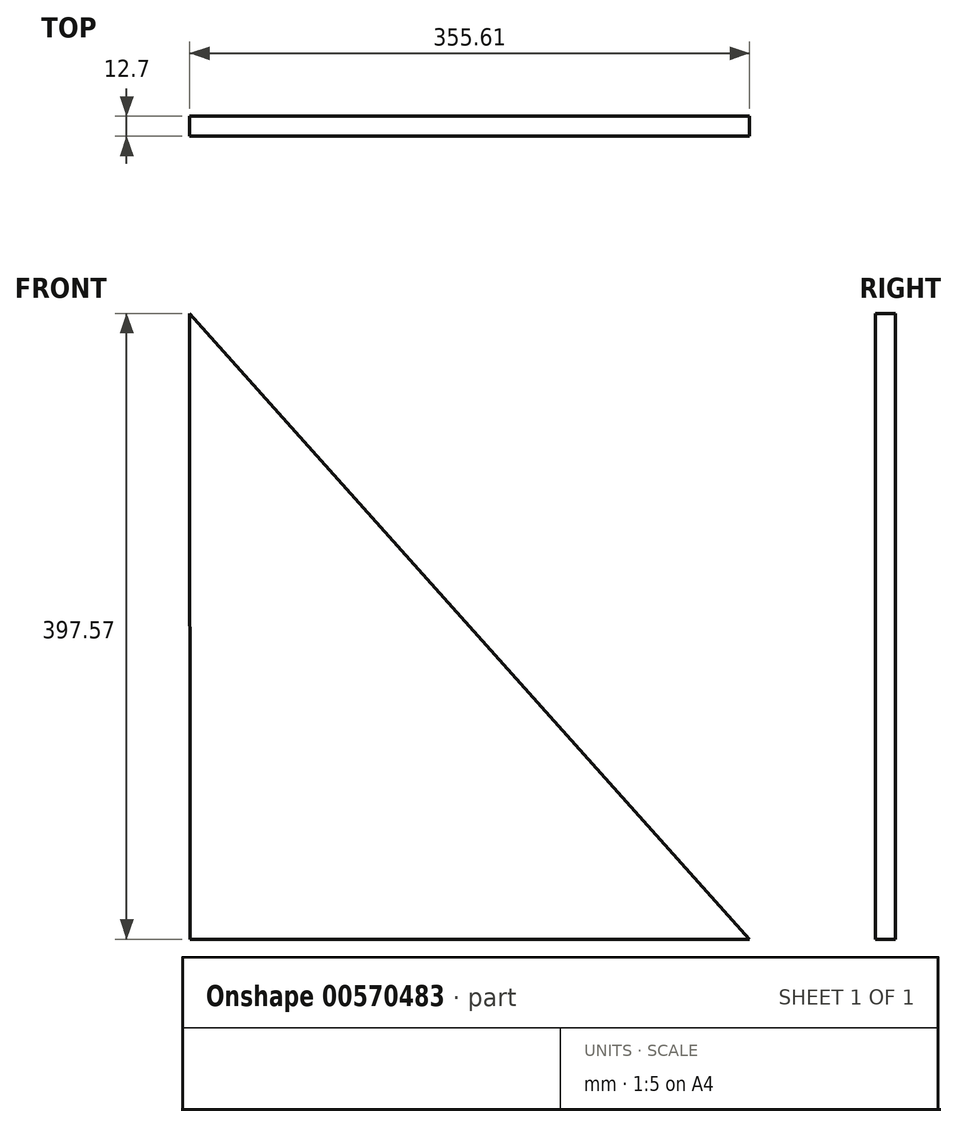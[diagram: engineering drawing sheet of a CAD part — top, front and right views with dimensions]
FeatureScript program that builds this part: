
annotation { "Feature Type Name" : "Feature", "Feature Type Description" : "" }
export const myFeature = defineFeature(function(context is Context, id is Id, definition is map)
    precondition{}
    {
        {
            var Q0;
            Q0=qCreatedBy(makeId("Front.planeOp"),FACE);
            var sketch = newSketch(context, id + "F0", { "sketchPlane" : qUnion([Q0])});
            skLineSegment(sketch, "E0.bottom", {"start": v(0, 0) * mm, "end": v(-355.6, 0) * mm});
            skLineSegment(sketch, "E0.right", {"start": v(-355.6, 0) * mm, "end": v(-355.6, 397.57) * mm});
            skLineSegment(sketch, "E1", {"start": v(-355.6, 397.57) * mm, "end": v(0, 0) * mm});
            skSolve(sketch);
        }
        {
            var Q0;
            Q0 = qSketchRegion(id + "F0", true);
            extrude(context, id + "F1", {"entities" : qUnion([Q0]), "depth" : 12.7 * mm, "offsetDistance" : 25.4 * mm});
        }
    });
